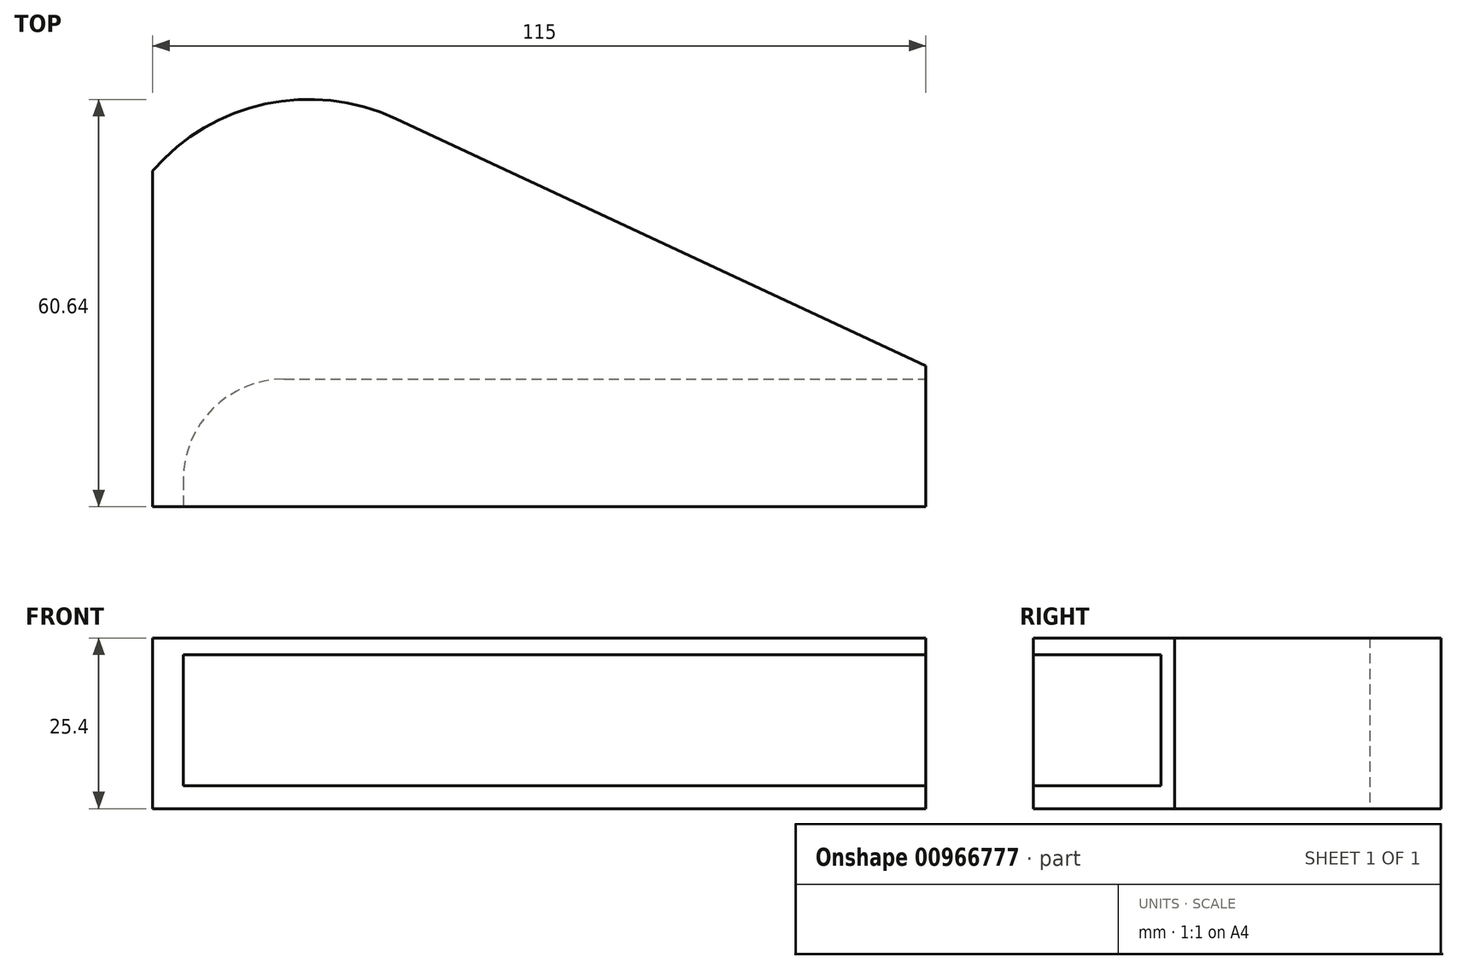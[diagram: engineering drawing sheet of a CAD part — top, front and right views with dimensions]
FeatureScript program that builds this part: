
annotation { "Feature Type Name" : "Feature", "Feature Type Description" : "" }
export const myFeature = defineFeature(function(context is Context, id is Id, definition is map)
    precondition{}
    {
        {
            var Q0;
            Q0=qCreatedBy(makeId("Top.planeOp"),FACE);
            var sketch = newSketch(context, id + "F0", { "sketchPlane" : qUnion([Q0])});
            skLineSegment(sketch, "E0", {"start": v(0, 0) * mm, "end": v(115, 0) * mm});
            skLineSegment(sketch, "E1", {"start": v(115, 0) * mm, "end": v(115, 21) * mm});
            skLineSegment(sketch, "E2", {"start": v(0, 0) * mm, "end": v(0, 50) * mm});
            skLineSegment(sketch, "E3", {"start": v(115, 21) * mm, "end": v(36.16, 57.77) * mm});
            skArc(sketch, "E4", {"start": v(36.16, 57.77) * mm, "mid": v(16.77, 59.95) * mm, "end": v(0, 50) * mm});
            skSolve(sketch);
        }
        {
            var Q0;
            Q0=qSketchRegion(id+"F0",true);
            extrude(context, id + "F1", {"entities" : qUnion([Q0]), "depth" : (1 * 25.4) * mm, "offsetDistance" : 25 * mm});
        }
        {
            var Q0;
            Q0=makeQuery(id+"F1.opExtrude","SWEPT_FACE",FACE,{"disambiguationData":[OSD([sQuery(id+"F0.wireOp",EDGE,"E0")])]});
            var sketch = newSketch(context, id + "F2", { "sketchPlane" : qUnion([Q0])});
            skLineSegment(sketch, "E5.bottom", {"start": v(4.55, 3.4) * mm, "end": v(115, 3.4) * mm});
            skLineSegment(sketch, "E5.top", {"start": v(4.55, 22.9) * mm, "end": v(115, 22.9) * mm});
            skLineSegment(sketch, "E5.left", {"start": v(4.55, 3.4) * mm, "end": v(4.55, 22.9) * mm});
            skLineSegment(sketch, "E5.right", {"start": v(115, 3.4) * mm, "end": v(115, 22.9) * mm});
            skSolve(sketch);
        }
        {
            var Q0;
            Q0=qSketchRegion(id+"F2",true);
            extrude(context, id + "F3", {"entities" : qUnion([Q0]), "operationType" : NewBodyOperationType.REMOVE, "oppositeDirection" : true, "depth" : 19 * mm, "offsetDistance" : 25 * mm});
        }
        {
            var Q0;
            Q0=makeQuery(id+"F3.boolean.opBoolean","COPY",EDGE,{"derivedFrom":makeQuery(id+"F3.opExtrude","CAP_EDGE",EDGE,{"disambiguationData":[OSD([sQuery(id+"F2.wireOp",EDGE,"E5.left")])],"isStart":false})});
            fillet(context, id + "F4", {"entities" : qUnion([Q0]), "radius" : 15 * mm, "tangentPropagation" : true, "allowEdgeOverflow" : false});
        }
    });
